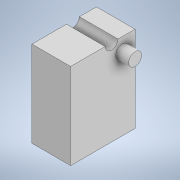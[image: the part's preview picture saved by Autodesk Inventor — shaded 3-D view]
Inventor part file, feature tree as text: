
AUTODESK INVENTOR PART (.ipt)
format: ipt  version: 2021 (Build 250183000, 183)  size: 160,768 bytes
history: native  units: mm
features: extrude x6, sketch x6, emboss x1
ambient origin geometry x8: Origin, YZ Plane, XZ Plane, XY Plane, X Axis, Y Axis, Z Axis, Center Point
bodies: Solid1 (feature_tree)
feature tree (13):
  extrude  "Extrusion1"  Depth=10.5655mm
  extrude  "Extrusion3"  Depth=9.0mm TaperAngle=0.0deg
  emboss  "Emboss1"
  extrude  "Extrusion5"  Depth=3.0mm TaperAngle=0.0deg
  extrude  "Extrusion6"  Depth=1.0mm
  extrude  "Extrusion9"  Depth=0.517mm TaperAngle=0.0deg
  extrude  "Extrusion10"  Depth=3.0mm
  sketch  "Sketch1"  dims[d0=21.131mm d2=10.5655mm]
  sketch  "Sketch4"  dims[d3=7.5mm d4=9.0mm d5=0.0mm]
  sketch  "Sketch6"  dims[d12=3.0mm d15=3.0mm d16=0.0mm]
  sketch  "Sketch7"  dims[d17=1.0mm d18=0.0mm d27=14.483mm]
  sketch  "Sketch10"  dims[d28=0.174mm d29=0.0mm d30=0.517mm d31=0.0mm]
  sketch  "Sketch11"  dims[d38=1.302mm d39=0.0mm d40=3.0mm d41=9.519mm d42=0.0mm d43=0.0mm]
